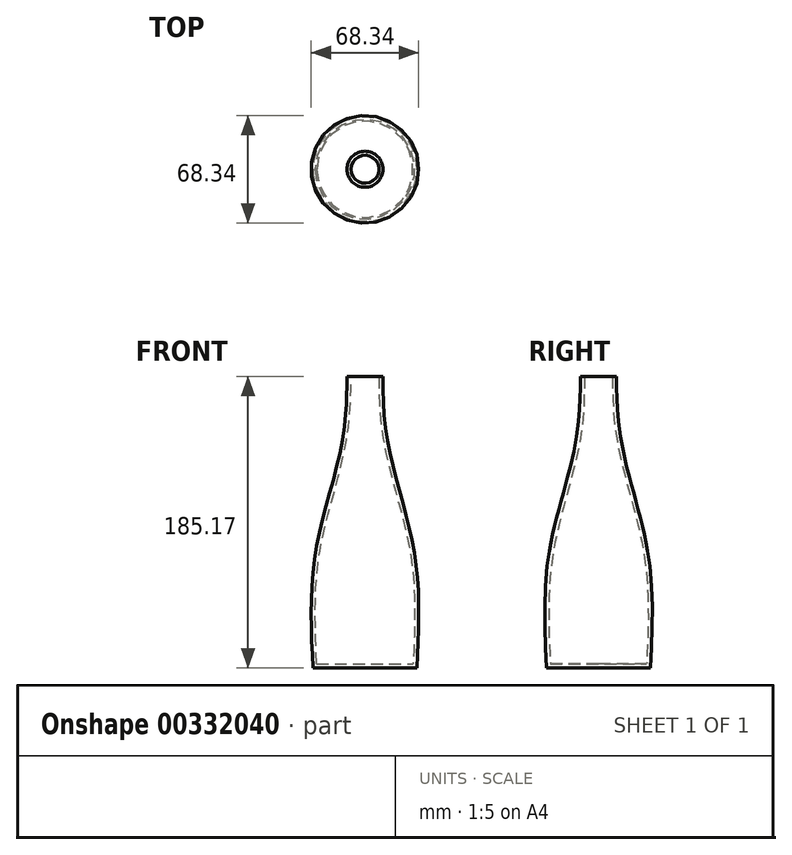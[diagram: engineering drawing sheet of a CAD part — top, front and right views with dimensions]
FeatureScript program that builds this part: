
annotation { "Feature Type Name" : "Feature", "Feature Type Description" : "" }
export const myFeature = defineFeature(function(context is Context, id is Id, definition is map)
    precondition{}
    {
        {
            var Q0;
            Q0=qCreatedBy(makeId("Top.planeOp"),FACE);
            var sketch = newSketch(context, id + "F0", { "sketchPlane" : qUnion([Q0])});
            skCircle(sketch, "E0", {"center": v(0, 0) * mm, "radius": 31.75 * mm});
            skSolve(sketch);
        }
        {
            var Q0;
            Q0=qCreatedBy(makeId("Top.planeOp"),FACE);
            cPlane(context, id + "F1", {"entities" : qUnion([Q0]), "cplaneType" : CPlaneType.OFFSET, "offset" : 84.84 * mm, "width" : 152.4 * mm, "height" : 152.4 * mm});
        }
        {
            var Q0;
            Q0=qCreatedBy(makeId("Top.planeOp"),FACE);
            cPlane(context, id + "F2", {"entities" : qUnion([Q0]), "cplaneType" : CPlaneType.OFFSET, "offset" : 71.12 * mm, "oppositeDirection" : true, "width" : 152.4 * mm, "height" : 152.4 * mm});
        }
        {
            var Q0;
            Q0=qCreatedBy(id+"F1.planeOp",FACE);
            cPlane(context, id + "F3", {"entities" : qUnion([Q0]), "cplaneType" : CPlaneType.OFFSET, "offset" : 29.2 * mm, "width" : 152.4 * mm, "height" : 152.4 * mm});
        }
        {
            var Q0;
            Q0=qCreatedBy(id+"F2.planeOp",FACE);
            var sketch = newSketch(context, id + "F4", { "sketchPlane" : qUnion([Q0])});
            skCircle(sketch, "E1", {"center": v(0, 0) * mm, "radius": 33.02 * mm});
            skSolve(sketch);
        }
        {
            var Q0;
            Q0=qCreatedBy(id+"F1.planeOp",FACE);
            var sketch = newSketch(context, id + "F5", { "sketchPlane" : qUnion([Q0])});
            skCircle(sketch, "E2", {"center": v(0, 0) * mm, "radius": 12.7 * mm});
            skSolve(sketch);
        }
        {
            var Q0;
            Q0=qCreatedBy(id+"F3.planeOp",FACE);
            var sketch = newSketch(context, id + "F6", { "sketchPlane" : qUnion([Q0])});
            skCircle(sketch, "E3", {"center": v(0, 0) * mm, "radius": 11.43 * mm});
            skSolve(sketch);
        }
        {
            var Q0;
            Q0=makeQuery(id+"F4.imprint","IMPRINT",FACE,{"disambiguationData":[TD([[makeQuery(id+"F4.imprint","IMPRINT",EDGE,{"derivedFrom":sQuery(id+"F4.wireOp",EDGE,"E1")}),1.0]])]});
            var Q1;
            Q1=makeQuery(id+"F0.imprint","IMPRINT",FACE,{"disambiguationData":[TD([[makeQuery(id+"F0.imprint","IMPRINT",EDGE,{"derivedFrom":sQuery(id+"F0.wireOp",EDGE,"E0")}),1.0]])]});
            var Q2;
            Q2=makeQuery(id+"F5.imprint","IMPRINT",FACE,{"disambiguationData":[TD([[makeQuery(id+"F5.imprint","IMPRINT",EDGE,{"derivedFrom":sQuery(id+"F5.wireOp",EDGE,"E2")}),1.0]])]});
            var Q3;
            Q3=makeQuery(id+"F6.imprint","IMPRINT",FACE,{"disambiguationData":[TD([[makeQuery(id+"F6.imprint","IMPRINT",EDGE,{"derivedFrom":sQuery(id+"F6.wireOp",EDGE,"E3")}),1.0]])]});
            loft(context, id + "F7", {"sheetProfilesArray" : [{ "sheetProfileEntities" : qUnion([Q0]) }, { "sheetProfileEntities" : qUnion([Q1]) }, { "sheetProfileEntities" : qUnion([Q2]) }, { "sheetProfileEntities" : qUnion([Q3]) }]});
        }
        {
            var Q0;
            Q0=makeQuery(id+"F7.opLoft","CAP_FACE",FACE,{"disambiguationData":[OSD([makeQuery(id+"F6.imprint","IMPRINT",FACE,{"disambiguationData":[TD([[makeQuery(id+"F6.imprint","IMPRINT",EDGE,{"derivedFrom":sQuery(id+"F6.wireOp",EDGE,"E3")}),1.0]])]})])],"isStart":true});
            shell(context, id + "F8", {"entities" : qUnion([Q0]), "thickness" : 2.54 * mm});
        }
    });
